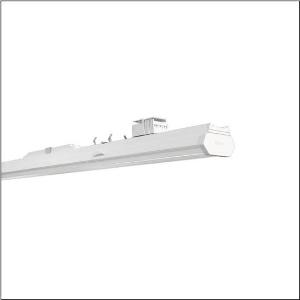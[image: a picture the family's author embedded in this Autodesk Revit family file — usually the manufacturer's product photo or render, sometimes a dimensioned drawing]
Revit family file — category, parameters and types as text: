
# Revit family: licross_21_protected_mo_52tp12dn4a5g3s
name_source: partatom
category: Lighting Fixtures
units: mm (PartAtom-declared; Revit-internal decimal feet)

## family parameters
Cut with Voids When Loaded = No
Host = Face
Light Source = No
Part Type = Normal
Room Calculation Point = No
Round Connector Dimension = Use Diameter
Shared = No

## types (1)
- --- (1 x LED, 940 lm, 6.8 W, 4000K)
    Apparent Load = 7 VA
    CIE Flux Codes = 73 92 98 99 100
    Color Rendering = 80
    Color Temperature = 4000K
    Default Elevation = 1800 mm
    Description = Licross 21 Protected MO, luminaire insert, of sheet steel, galvanised, coil coated, white, length: 1.500mm, width: 90mm, height: 103mm, LED rated luminous flux: 10.700lm, light colour: 840, SDCM (Standard Deviation of Colour Matching)MacAdam ≤ 3 SDCM (initial), control gear: DALI 2 (for two DALI lines), with plug, 6-pole, with phase selection, for trunking rail, 14-core, mains connection: 220..240V, AC, 50/60Hz, rated input power: 66W, for trunking rail, 14-core, internal wiring halogen-free, for emergency light function, converter,control gear: single battery element, battery: LiFePO4, 9Ah, primary light control with lens, of plastic, primary optical cover: cover, of PMMA, light emission: direct distribution, primary light characteristic: symmetric, protection rating (complete): IP64, insulation class (complete): insulation class I (protective earthing), certification: CE, UKCA, protection symbol: D if used in an environment with conductive dust loads with corresponding accessories, impact resistance: IK06, permissible ambient temperature for indoor applications: +5..+35°C, standard: EN 60598-2-22, LABS conformity tested according to VDMA 24364:2018-05, reducing of maximum allowable ambient temperature of 5°C with ceiling mounting, corresponds to IFS (International Featured Standards) requirements for safety and quality in the food industry, The light source and the operating device comply with the requirements of the Ecodesign Regulation (EU) 2019/2020 and are replaceable in accordance with this regulation, packaging unit: 1 piece
    Height = 92 mm
    Lamp = 1 x LED
    Lamp Light Flux = 940 lm
    Lamp Power = 6.8 W
    Lamp count = 1
    Length = 1500 mm
    Luminous efficacy = 138 lm/W
    Manufacturer = Siteco
    ModVariant = No
    Model = 52TP12DN4A5G3S
    Mounting Place = Ceiling
    Mounting Type = Pendant
    Number of Poles = 1
    OnlyDefault = Yes
    Power Factor = 1
    Product Name = Licross 21 Protected MO
    Product group = luminaire insert | ceiling pendant
    ProductGroupID = 901
    Protection Class = Protection class I
    Protection Degree = IP 64
    RLX_Detail_Level = 1
    RLX_Emergency_Light_Flux = 0 lm
    RLX_Emergency_Type = 0
    RLX_Emergency_Type_DB = No
    RlxData = <blob elided: 25181 chars, md5=fc14ea5f>
    Socket = socket
    Standby Power = 0 W
    System Light Flux = 940 lm
    System Power = 7 W
    Type Comments = : emergency light operation: 3 h
    Type Image = l_1256148.jpg
    URL = http://relux.com
    VarID = @adj_112437
    Voltage = 0 V
    Weight = 0.00 kg
    Width = 88 mm

## geometry (parser evidence)
native form markers: Blend x4, Sweep x9
no freeform markers — native parametric forms only
